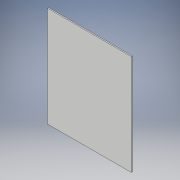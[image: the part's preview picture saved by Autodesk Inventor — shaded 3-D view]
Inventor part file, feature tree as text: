
AUTODESK INVENTOR PART (.ipt)
format: ipt  version: 2017 (Build 210142000, 142)  size: 88,576 bytes
history: native  units: in
note: dims shown in document units (in); Inventor stores cm internally (conversion verified against a paired STEP export)
features: extrude x1, sketch x1
ambient origin geometry x8: Origin, YZ Plane, XZ Plane, XY Plane, X Axis, Y Axis, Z Axis, Center Point
bodies: Solid1 (feature_tree)
feature tree (2):
  extrude  "Extrusion1"  Depth=43.0in
  sketch  "Sketch1"  dims[d0=36.0in d1=43.0in d2=0.5in d3=0.0in]
